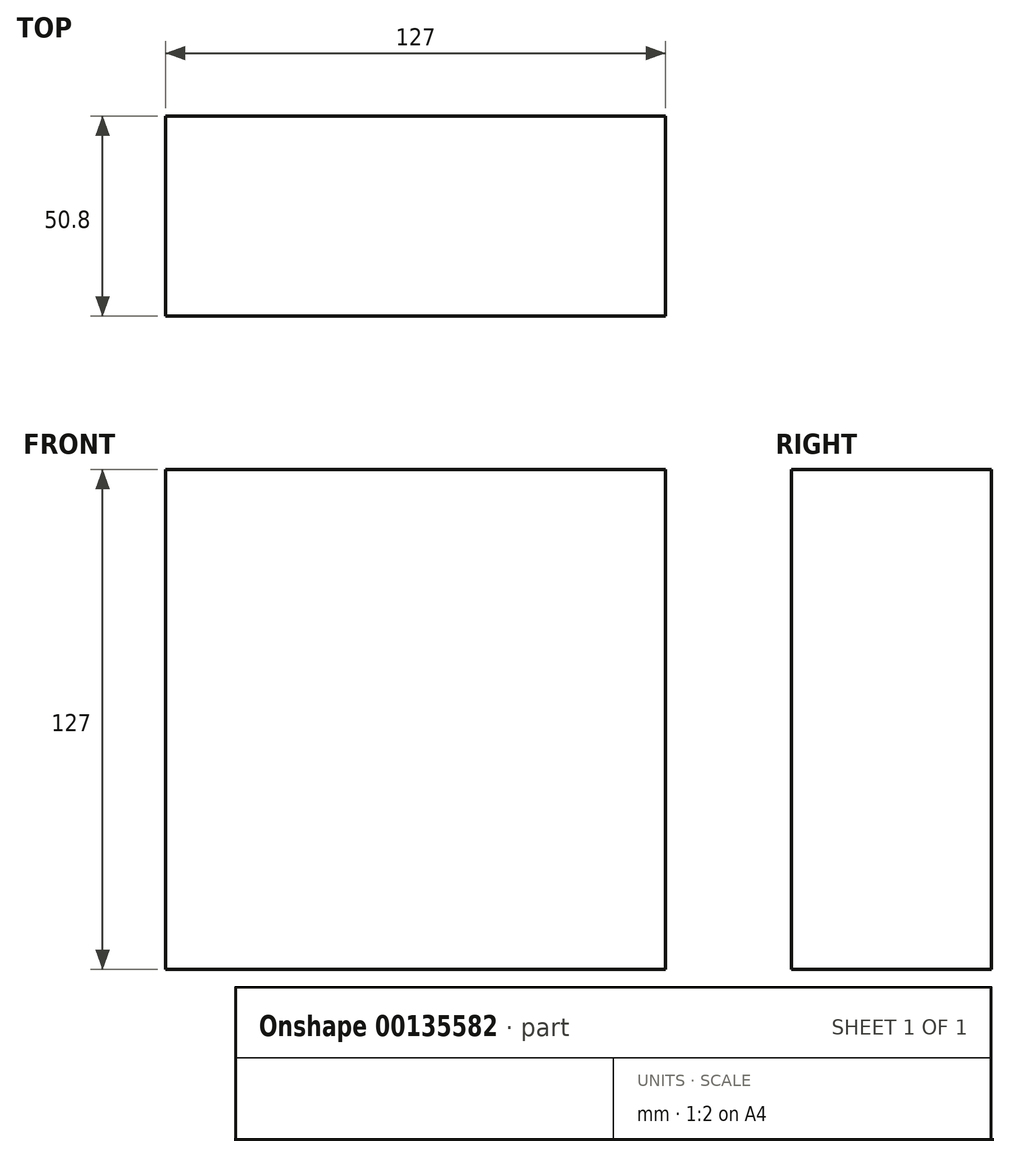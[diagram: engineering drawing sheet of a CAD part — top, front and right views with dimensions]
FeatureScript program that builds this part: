
annotation { "Feature Type Name" : "Feature", "Feature Type Description" : "" }
export const myFeature = defineFeature(function(context is Context, id is Id, definition is map)
    precondition{}
    {
        {
            var Q0;
            Q0=qCreatedBy(makeId("Front.planeOp"),FACE);
            var sketch = newSketch(context, id + "F0", { "sketchPlane" : qUnion([Q0])});
            skLineSegment(sketch, "E0", {"start": v(-103.87, 93.6) * mm, "end": v(23.13, 93.6) * mm});
            skLineSegment(sketch, "E1", {"start": v(23.13, 93.6) * mm, "end": v(23.13, -33.4) * mm});
            skLineSegment(sketch, "E2", {"start": v(23.13, -33.4) * mm, "end": v(-103.87, -33.4) * mm});
            skLineSegment(sketch, "E3", {"start": v(-103.87, -33.4) * mm, "end": v(-103.87, 93.6) * mm});
            skSolve(sketch);
        }
        {
            var Q0;
            Q0 = qSketchRegion(id + "F0", true);
            extrude(context, id + "F1", {"entities" : qUnion([Q0]), "depth" : 50.8 * mm});
        }
    });
